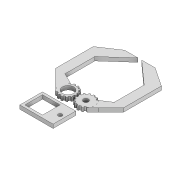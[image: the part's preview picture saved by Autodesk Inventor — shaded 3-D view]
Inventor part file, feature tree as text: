
AUTODESK INVENTOR PART (.ipt)
format: ipt  version: 2021 (Build 250183000, 183)  size: 280,064 bytes
history: native  units: mm
features: extrude x2, sketch x2, other x1
ambient origin geometry x8: Origin, YZ Plane, XZ Plane, XY Plane, X Axis, Y Axis, Z Axis, Center Point
bodies: Body1 (feature_tree)
feature tree (5):
  other  "Sólido1"
  extrude  "Extrusión1"  Depth=140.0mm TaperAngle=360.0deg
  extrude  "Extrusión2"  Depth=3.0mm
  sketch  "Boceto1"  dims[d0=12.0mm d4=140.0mm d6=360.0deg]
  sketch  "Boceto2"  dims[d9=0.2mm d12=140.0mm d14=4.0mm d15=2.0mm d16=4.0mm d24=3.0mm d25=0.0mm d26=14.0mm d27=7.0mm d28=7.0mm d29=14.0mm d30=14.0mm d31=14.0mm d32=3.0mm d33=2.0mm d34=9.0mm d35=9.0mm d36=3.0mm d37=0.0mm]
